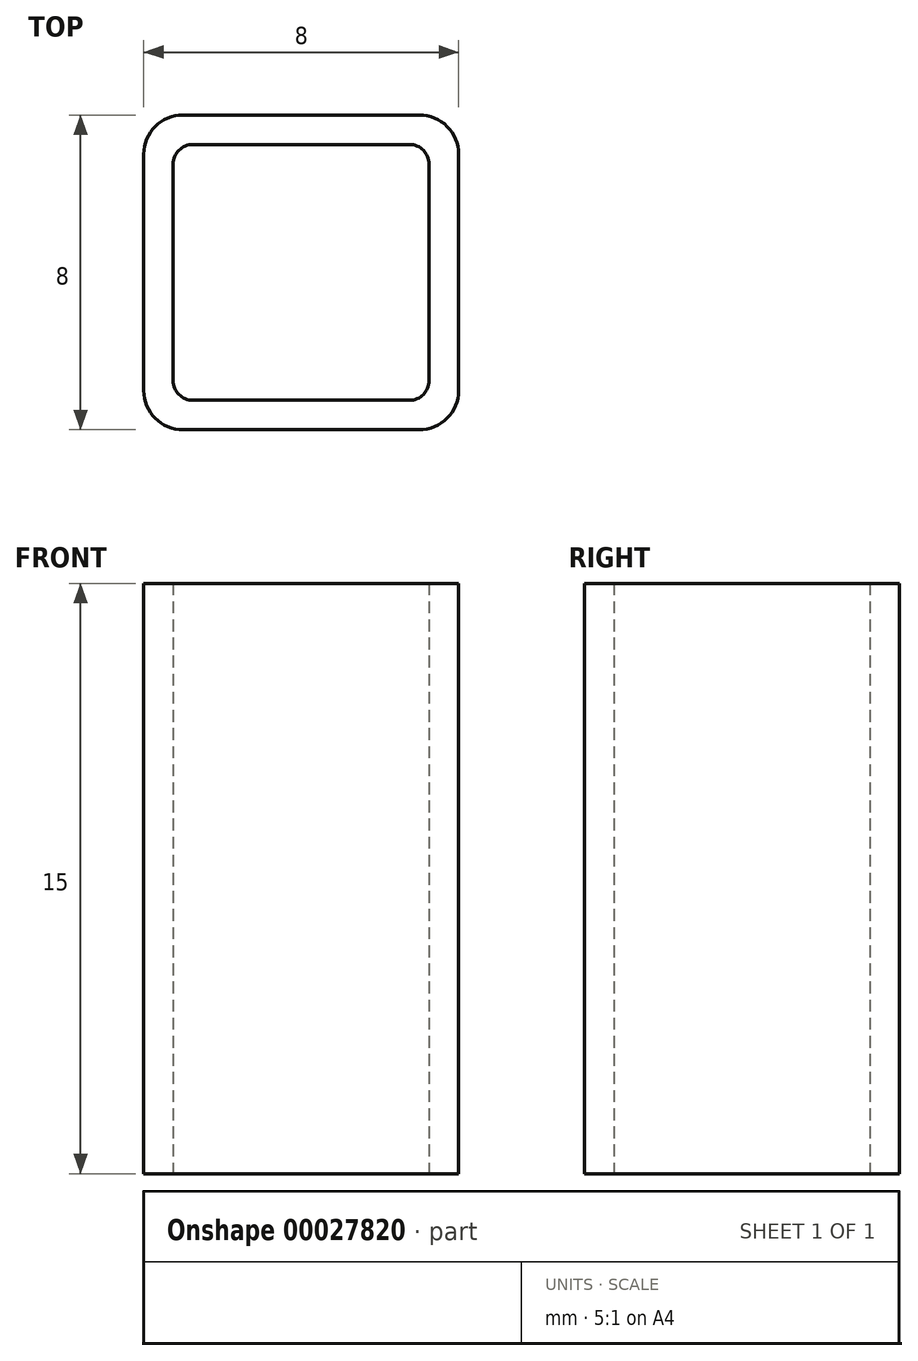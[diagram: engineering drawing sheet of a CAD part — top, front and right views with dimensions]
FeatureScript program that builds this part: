
annotation { "Feature Type Name" : "Feature", "Feature Type Description" : "" }
export const myFeature = defineFeature(function(context is Context, id is Id, definition is map)
    precondition{}
    {
        {
            var Q0;
            Q0=qCreatedBy(makeId("Top.planeOp"),FACE);
            var sketch = newSketch(context, id + "F0", { "sketchPlane" : qUnion([Q0])});
            skLineSegment(sketch, "E0.rect.bottom", {"start": v(4, -4) * mm, "end": v(-4, -4) * mm});
            skLineSegment(sketch, "E0.rect.top", {"start": v(4, 4) * mm, "end": v(-4, 4) * mm});
            skLineSegment(sketch, "E0.rect.left", {"start": v(4, -4) * mm, "end": v(4, 4) * mm});
            skLineSegment(sketch, "E0.rect.right", {"start": v(-4, -4) * mm, "end": v(-4, 4) * mm});
            skPoint(sketch, "E0.rect.middle", {"position": v(0, 0) * mm});
            skLineSegment(sketch, "E1.rect.bottom", {"start": v(3.25, -3.25) * mm, "end": v(-3.25, -3.25) * mm});
            skLineSegment(sketch, "E1.rect.top", {"start": v(3.25, 3.25) * mm, "end": v(-3.25, 3.25) * mm});
            skLineSegment(sketch, "E1.rect.left", {"start": v(3.25, -3.25) * mm, "end": v(3.25, 3.25) * mm});
            skLineSegment(sketch, "E1.rect.right", {"start": v(-3.25, -3.25) * mm, "end": v(-3.25, 3.25) * mm});
            skSolve(sketch);
        }
        {
            var Q0;
            Q0=makeQuery(id+"F0.imprint","IMPRINT",FACE,{"disambiguationData":[TD([[makeQuery(id+"F0.imprint","IMPRINT",EDGE,{"derivedFrom":sQuery(id+"F0.wireOp",EDGE,"E0.rect.bottom")}),-1.0]])]});
            extrude(context, id + "F1", {"entities" : qUnion([Q0]), "depth" : 15 * mm});
        }
        {
            var Q0;
            Q0=makeQuery(id+"F1.opExtrude","SWEPT_EDGE",EDGE,{"disambiguationData":[OSD([sQuery(id+"F0.wireOp",EDGE,"E0.rect.bottom"),sQuery(id+"F0.wireOp",EDGE,"E0.rect.right")])]});
            var Q1;
            Q1=makeQuery(id+"F1.opExtrude","SWEPT_EDGE",EDGE,{"disambiguationData":[OSD([sQuery(id+"F0.wireOp",EDGE,"E0.rect.bottom"),sQuery(id+"F0.wireOp",EDGE,"E0.rect.left")])]});
            var Q2;
            Q2=makeQuery(id+"F1.opExtrude","SWEPT_EDGE",EDGE,{"disambiguationData":[OSD([sQuery(id+"F0.wireOp",EDGE,"E0.rect.top"),sQuery(id+"F0.wireOp",EDGE,"E0.rect.right")])]});
            var Q3;
            Q3=makeQuery(id+"F1.opExtrude","SWEPT_EDGE",EDGE,{"disambiguationData":[OSD([sQuery(id+"F0.wireOp",EDGE,"E0.rect.top"),sQuery(id+"F0.wireOp",EDGE,"E0.rect.left")])]});
            fillet(context, id + "F2", {"entities" : qUnion([Q0, Q1, Q2, Q3]), "radius" : 1 * mm, "tangentPropagation" : true, "allowEdgeOverflow" : false});
        }
        {
            var Q0;
            Q0=makeQuery(id+"F1.opExtrude","SWEPT_EDGE",EDGE,{"disambiguationData":[OSD([sQuery(id+"F0.wireOp",EDGE,"E1.rect.top"),sQuery(id+"F0.wireOp",EDGE,"E1.rect.left")])]});
            var Q1;
            Q1=makeQuery(id+"F1.opExtrude","SWEPT_EDGE",EDGE,{"disambiguationData":[OSD([sQuery(id+"F0.wireOp",EDGE,"E1.rect.bottom"),sQuery(id+"F0.wireOp",EDGE,"E1.rect.left")])]});
            var Q2;
            Q2=makeQuery(id+"F1.opExtrude","SWEPT_EDGE",EDGE,{"disambiguationData":[OSD([sQuery(id+"F0.wireOp",EDGE,"E1.rect.bottom"),sQuery(id+"F0.wireOp",EDGE,"E1.rect.right")])]});
            var Q3;
            Q3=makeQuery(id+"F1.opExtrude","SWEPT_EDGE",EDGE,{"disambiguationData":[OSD([sQuery(id+"F0.wireOp",EDGE,"E1.rect.top"),sQuery(id+"F0.wireOp",EDGE,"E1.rect.right")])]});
            fillet(context, id + "F3", {"entities" : qUnion([Q0, Q1, Q2, Q3]), "radius" : 0.5 * mm, "tangentPropagation" : true, "allowEdgeOverflow" : false});
        }
    });
